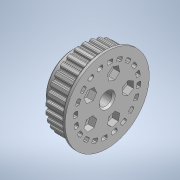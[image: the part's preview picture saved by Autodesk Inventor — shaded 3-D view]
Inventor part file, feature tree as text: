
AUTODESK INVENTOR PART (.ipt)
format: ipt  version: 2020 (Build 240168000, 168)  size: 2,001,920 bytes
history: native  units: mm (DEFAULTED — no unit token found)
features: extrude x11, sketch x11, projected_geometry x9, plane x5, pattern_circular x5, thicken_offset x4, chamfer x4, fillet x3, other x3, revolve x1, hole x1, reference x1
ambient origin geometry x8: Origin, YZ Plane, XZ Plane, XY Plane, X Axis, Y Axis, Z Axis, Center Point
bodies: Solid1 (feature_tree)
feature tree (58):
  revolve  "Revolution1"  [1 undecoded]
  hole  "Hole1"  [1 undecoded]
  extrude  "Extrusion1"  TaperAngle=0.0deg  [1 undecoded]
  plane  "Work Plane1"
  extrude  "Extrusion2"  Depth=5.0mm TaperAngle=0.0deg
  plane  "Work Plane2"
  extrude  "Extrusion3"  Depth=10.0mm TaperAngle=0.0deg
  extrude  "Extrusion5"  Depth=35.15mm
  sketch  "Sketch8"  dims[d15=70.0mm d16=5.0mm d17=0.0mm]
  plane  "Work Plane3"
  extrude  "Extrusion6"  Depth=54.0mm
  sketch  "Sketch9"  dims[d25=8.0mm d26=10.0mm d27=0.0mm]
  plane  "Work Plane4"
  extrude  "Extrusion7"  Depth=2.0mm
  sketch  "Sketch10"  dims[d28=10.0mm d29=0.0mm d30=35.15mm]
  plane  "Work Plane5"
  extrude  "Extrusion8"  Depth=13.0mm
  thicken_offset  "Thicken1"
  extrude  "Extrusion9"  Depth=10.0mm TaperAngle=0.0deg
  extrude  "Extrusion10"  Depth=4.05mm
  pattern_circular  "Circular Pattern2"  Angle=30.0deg  [1 undecoded]
  thicken_offset  "Thicken2"
  chamfer  "Chamfer1"  Distance=60.0mm Angle=360.0deg
  chamfer  "Chamfer2"  Distance=4.0mm
  chamfer  "Chamfer3"  Distance=50.0mm Angle=360.0deg
  extrude  "Extrusion12"  Depth=0.7mm
  pattern_circular  "Circular Pattern4"  Angle=45.0deg  [1 undecoded]
  fillet  "Fillet3"  Radius=1.0mm
  pattern_circular  "Circular Pattern5"  Angle=45.0deg  [1 undecoded]
  thicken_offset  "Thicken3"
  chamfer  "Chamfer4"  Distance=37.0mm
  extrude  "Extrusion13"  Depth=42.0mm
  pattern_circular  "Circular Pattern6"  [2 undecoded]
  fillet  "Fillet4"  Radius=200.0mm
  fillet  "Fillet5"  Radius=200.0mm
  pattern_circular  "Circular Pattern7"  [2 undecoded]
  thicken_offset  "Thicken5"
  sketch  "Sketch2"  dims[d0=360.0deg]
  sketch  "Sketch4"  dims[d1=10.0mm d2=6.0mm d3=4.0mm d4=2.0mm d5=90.0deg d6=12.5mm d7=0.0mm d8=7.5mm d9=0.0mm]
  sketch  "Sketch5"  dims[d10=0.0mm d11=70.0mm]
  sketch  "Sketch7"  dims[d12=5.0mm d13=0.0mm d14=0.0mm]
  projected_geometry  "Projected Loop2"
  projected_geometry  "Projected Loop3"
  reference  "Reference1"
  projected_geometry  "Projected Loop4"
  sketch  "Sketch11"  dims[d31=10.0mm d32=0.0mm d33=54.0mm]
  projected_geometry  "Projected Loop5"
  sketch  "Sketch12"  dims[d34=10.0mm d35=0.0mm d36=2.0mm]
  projected_geometry  "Projected Loop6"
  sketch  "Sketch14"  dims[d37=2.0mm d38=13.0mm]
  projected_geometry  "Projected Loop8"
  projected_geometry  "Projected Loop9"
  projected_geometry  "Projected Loop10"
  sketch  "Sketch15"  dims[d39=4.2mm d40=10.0mm d41=0.0mm d42=4.05mm d43=30.0deg d44=60.0mm d46=360.0deg d48=4.0mm d49=0.0mm d50=50.0mm d51=360.0deg d53=0.7mm d54=1.0mm d66=1.0mm d67=2.0mm d68=45.0deg d69=1.0mm d70=2.0mm d71=45.0deg d72=1.0mm d73=2.0mm d74=45.0deg d75=37.0mm d76=42.0mm d77=1.745329mm d78=200.0mm d79=0.0mm d80=200.0mm d81=360.0deg d83=0.6mm d84=200.0mm d85=360.0deg d87=0.5mm d88=0.5mm d89=1.0mm d90=2.0mm d91=45.0deg d92=2.5mm d93=3.0mm d94=5.0mm d95=8.0mm d96=5.0mm d97=8.0mm d98=3.0mm d99=3.0mm d100=15.5mm d101=0.0mm d102=50.0mm d103=360.0deg d105=0.5mm d106=1.0mm d107=1.0mm d108=50.0mm d109=360.0deg d113=0.025mm d114=0.025mm]
  projected_geometry  "Projected Loop11"
  parser-record x1  (decoder bookkeeping rows leaked as tree rows — omitted from the tree; the rows remain in map.json)
  other  "reducer_3.iam"
  other  "bearing_35_44_5:1"
note: 10 required parameter values undecoded (feature->parameter linkage not recoverable at this tier; creation-order binding heuristic only, values carry confidence <= 0.55)
note: 1 file-system path scrubbed to <path> (originals preserved in map.json)